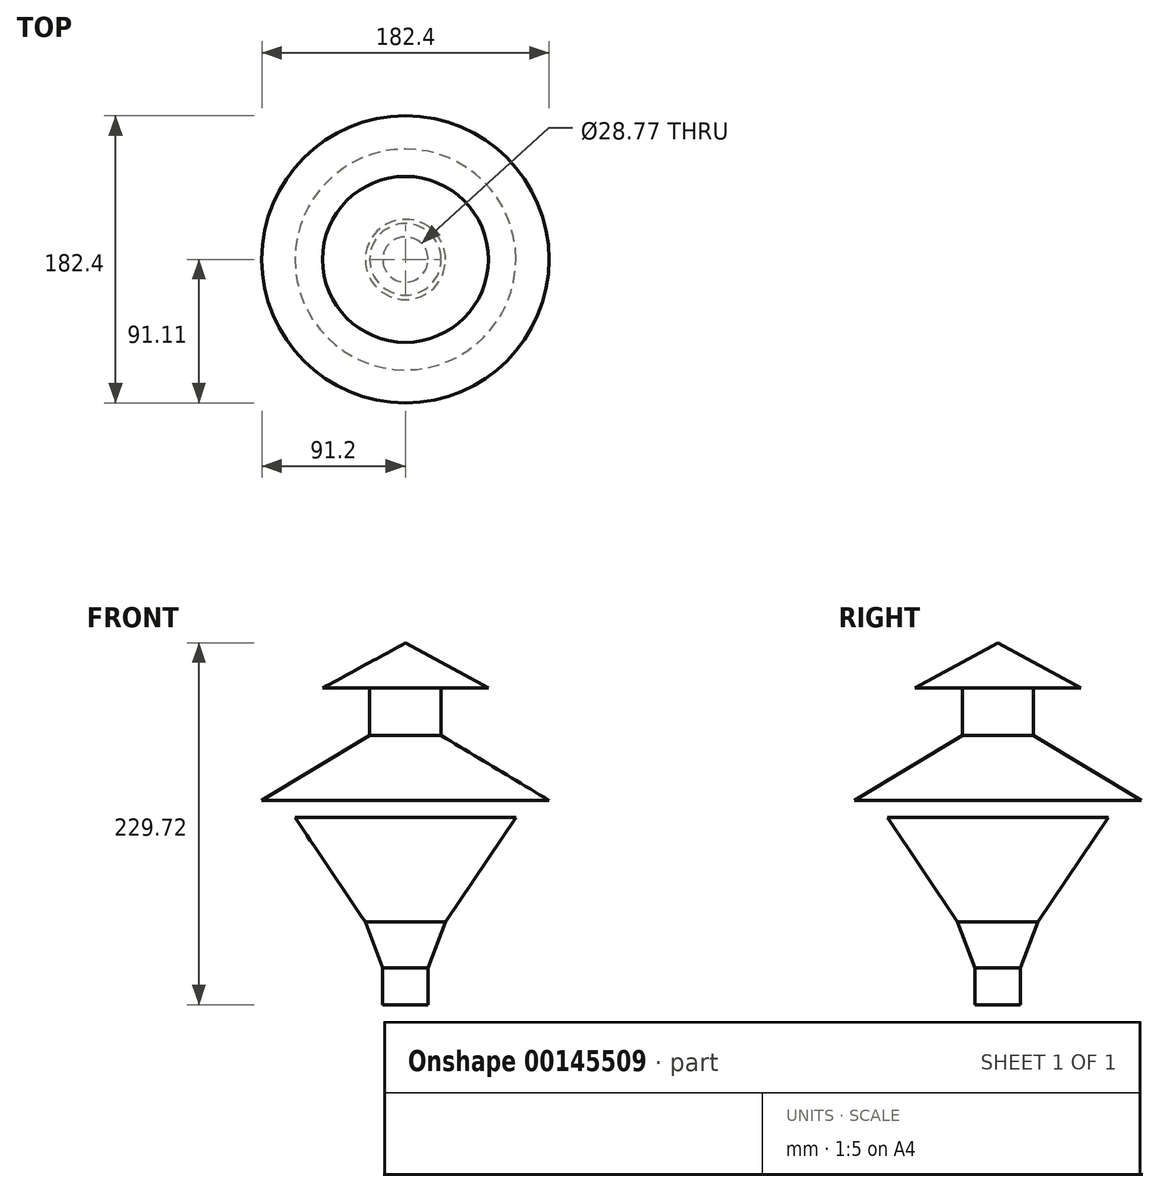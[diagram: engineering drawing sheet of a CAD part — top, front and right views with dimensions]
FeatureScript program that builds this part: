
annotation { "Feature Type Name" : "Feature", "Feature Type Description" : "" }
export const myFeature = defineFeature(function(context is Context, id is Id, definition is map)
    precondition{}
    {
        {
            var Q0;
            Q0=qCreatedBy(makeId("Front.planeOp"),FACE);
            cPlane(context, id + "F0", {"entities" : qUnion([Q0]), "cplaneType" : CPlaneType.OFFSET, "offset" : 25.4 * mm, "width" : 152.4 * mm, "height" : 152.4 * mm});
        }
        {
            var Q0;
            Q0=qCreatedBy(id+"F0.planeOp",FACE);
            var sketch = newSketch(context, id + "F1", { "sketchPlane" : qUnion([Q0])});
            skLineSegment(sketch, "E0", {"start": v(0, 0) * mm, "end": v(0, 100) * mm, "construction": true});
            skLineSegment(sketch, "E1", {"start": v(0, 100) * mm, "end": v(52.7, 71.32) * mm});
            skLineSegment(sketch, "E2", {"start": v(52.7, 71.32) * mm, "end": v(22.7, 71.32) * mm});
            skLineSegment(sketch, "E3", {"start": v(22.7, 71.32) * mm, "end": v(22.7, 41.32) * mm});
            skLineSegment(sketch, "E4", {"start": v(22.7, 41.32) * mm, "end": v(91.2, 0) * mm});
            skLineSegment(sketch, "E5.MirrorCS", {"start": v(-52.7, 71.32) * mm, "end": v(-22.7, 71.32) * mm});
            skLineSegment(sketch, "E6.MirrorCS", {"start": v(-22.7, 71.32) * mm, "end": v(-22.7, 41.32) * mm});
            skLineSegment(sketch, "E7.MirrorCS", {"start": v(0, 100) * mm, "end": v(-52.7, 71.32) * mm});
            skLineSegment(sketch, "E8.MirrorCS", {"start": v(-22.7, 41.32) * mm, "end": v(-91.2, 0) * mm});
            skSolve(sketch);
        }
        {
            var Q0;
            Q0=sQuery(id+"F1.wireOp",EDGE,"E1");
            var Q1;
            Q1=sQuery(id+"F1.wireOp",EDGE,"E2");
            var Q2;
            Q2=sQuery(id+"F1.wireOp",EDGE,"E3");
            var Q3;
            Q3=sQuery(id+"F1.wireOp",EDGE,"E4");
            var Q4;
            Q4=sQuery(id+"F1.wireOp",EDGE,"E0");
            revolve(context, id + "F2", {"bodyType" : ToolBodyType.SURFACE, "surfaceEntities" : qUnion([Q0, Q1, Q2, Q3]), "axis" : qUnion([Q4]), "revolveType" : RevolveType.FULL});
        }
        {
            var Q0;
            Q0=qCreatedBy(makeId("Right.planeOp"),FACE);
            var sketch = newSketch(context, id + "F3", { "sketchPlane" : qUnion([Q0])});
            skLineSegment(sketch, "E9", {"start": v(-25.5, -10.78) * mm, "end": v(-25.5, -110.78) * mm, "construction": true});
            skLineSegment(sketch, "E10", {"start": v(44.64, -10.78) * mm, "end": v(0, -77.27) * mm});
            skLineSegment(sketch, "E11", {"start": v(0, -77.27) * mm, "end": v(-11.1, -106.34) * mm});
            skLineSegment(sketch, "E12", {"start": v(-11.1, -106.34) * mm, "end": v(-11.1, -129.72) * mm});
            skLineSegment(sketch, "E13.MirrorCS", {"start": v(-95.62, -10.78) * mm, "end": v(-50.98, -77.27) * mm});
            skLineSegment(sketch, "E14.MirrorCS", {"start": v(-39.88, -106.34) * mm, "end": v(-39.88, -129.72) * mm});
            skLineSegment(sketch, "E15.MirrorCS", {"start": v(-50.98, -77.27) * mm, "end": v(-39.88, -106.34) * mm});
            skSolve(sketch);
        }
        {
            var Q0;
            Q0=sQuery(id+"F3.wireOp",EDGE,"E10");
            var Q1;
            Q1=sQuery(id+"F3.wireOp",EDGE,"E11");
            var Q2;
            Q2=sQuery(id+"F3.wireOp",EDGE,"E12");
            var Q3;
            Q3=sQuery(id+"F3.wireOp",EDGE,"E9");
            revolve(context, id + "F4", {"bodyType" : ToolBodyType.SURFACE, "surfaceEntities" : qUnion([Q0, Q1, Q2]), "axis" : qUnion([Q3]), "revolveType" : RevolveType.FULL});
        }
    });
